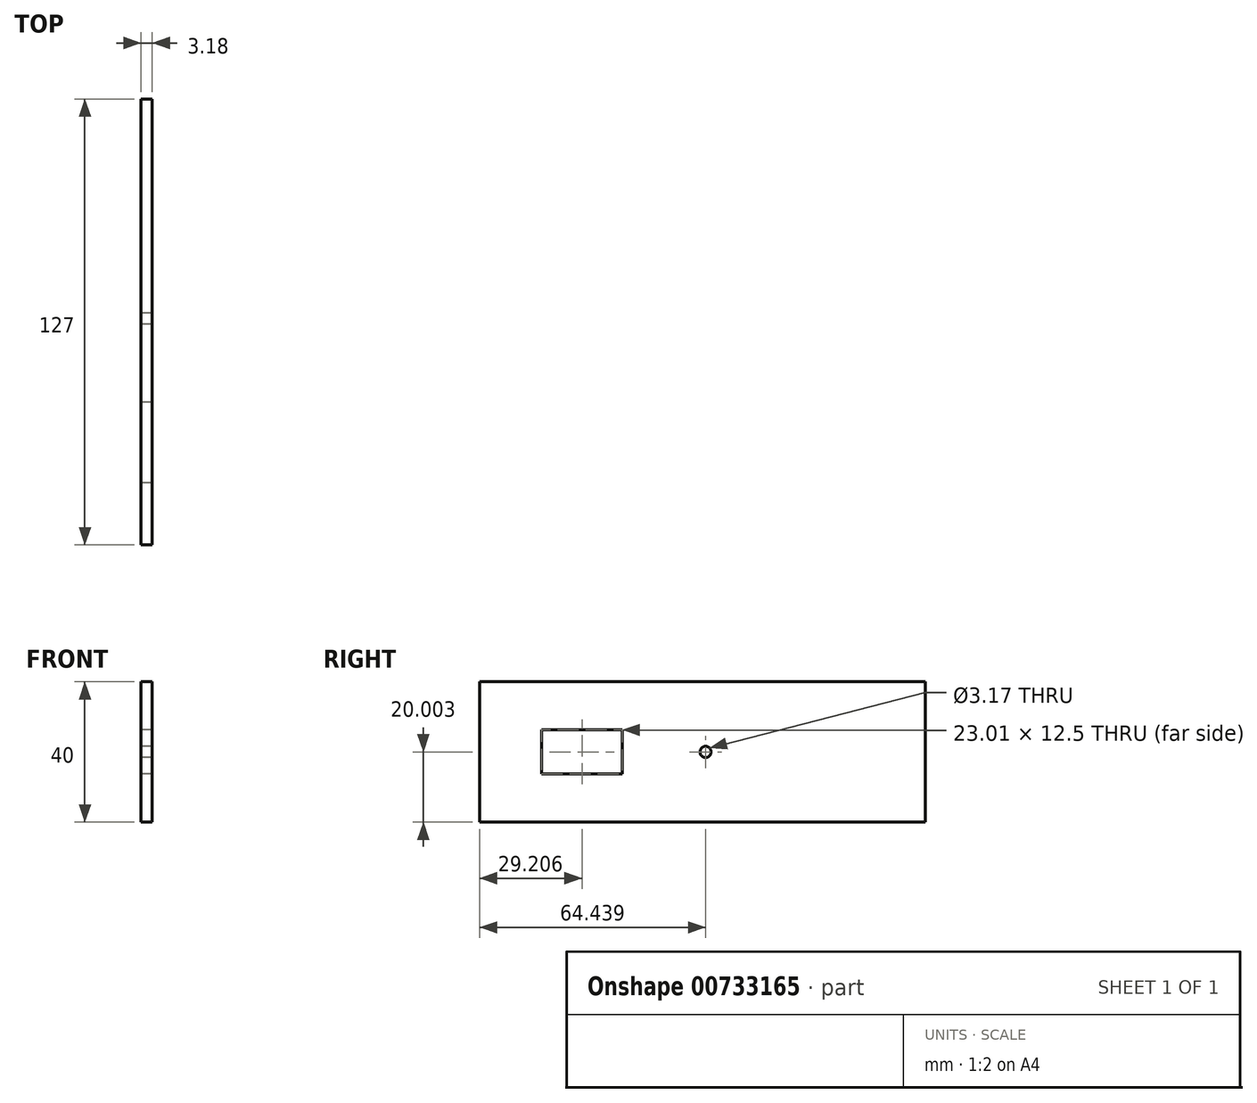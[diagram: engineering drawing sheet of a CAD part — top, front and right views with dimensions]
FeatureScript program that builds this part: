
annotation { "Feature Type Name" : "Feature", "Feature Type Description" : "" }
export const myFeature = defineFeature(function(context is Context, id is Id, definition is map)
    precondition{}
    {
        {
            var Q0;
            Q0=qCreatedBy(makeId("Right.planeOp"),FACE);
            var sketch = newSketch(context, id + "F0", { "sketchPlane" : qUnion([Q0])});
            skLineSegment(sketch, "E0.bottom", {"start": v(0, 0) * mm, "end": v(127, 0) * mm});
            skLineSegment(sketch, "E0.top", {"start": v(0, 40) * mm, "end": v(127, 40) * mm});
            skLineSegment(sketch, "E0.left", {"start": v(0, 0) * mm, "end": v(0, 40) * mm});
            skLineSegment(sketch, "E0.right", {"start": v(127, 0) * mm, "end": v(127, 40) * mm});
            skLineSegment(sketch, "E1", {"start": v(0, 0) * mm, "end": v(0, 20) * mm});
            skLineSegment(sketch, "E2", {"start": v(0, 20) * mm, "end": v(127, 20) * mm});
            skLineSegment(sketch, "E3", {"start": v(0, 20) * mm, "end": v(5, 20) * mm});
            skLineSegment(sketch, "E4", {"start": v(127, 20) * mm, "end": v(122, 20) * mm});
            skLineSegment(sketch, "E5", {"start": v(5, 20) * mm, "end": v(17.7, 20) * mm});
            skLineSegment(sketch, "E6", {"start": v(17.7, 20) * mm, "end": v(17.7, 26.25) * mm});
            skLineSegment(sketch, "E7", {"start": v(17.7, 26.25) * mm, "end": v(40.71, 26.25) * mm});
            skLineSegment(sketch, "E8", {"start": v(40.71, 26.25) * mm, "end": v(40.71, 13.75) * mm});
            skLineSegment(sketch, "E9", {"start": v(40.71, 13.75) * mm, "end": v(17.7, 13.75) * mm});
            skLineSegment(sketch, "E10", {"start": v(17.7, 13.75) * mm, "end": v(17.7, 20) * mm});
            skLineSegment(sketch, "E11", {"start": v(17.7, 20) * mm, "end": v(29.2, 20) * mm});
            skLineSegment(sketch, "E12", {"start": v(29.2, 20) * mm, "end": v(39.2, 20) * mm});
            skLineSegment(sketch, "E13", {"start": v(39.2, 20) * mm, "end": v(59.2, 20) * mm});
            skLineSegment(sketch, "E14", {"start": v(17.7, 13.75) * mm, "end": v(34.44, 13.75) * mm});
            skLineSegment(sketch, "E15", {"start": v(34.44, 13.75) * mm, "end": v(34.44, 20) * mm});
            skLineSegment(sketch, "E16", {"start": v(34.44, 20) * mm, "end": v(44.44, 20) * mm});
            skLineSegment(sketch, "E17", {"start": v(44.44, 20) * mm, "end": v(64.44, 20) * mm});
            skCircle(sketch, "E18", {"center": v(64.44, 20) * mm, "radius": 1.59 * mm});
            skSolve(sketch);
        }
        {
            var Q0;
            Q0 = qSketchRegion(id + "F0", true);
            extrude(context, id + "F1", {"entities" : qUnion([Q0]), "depth" : 3.17 * mm, "offsetDistance" : 25.4 * mm});
        }
    });
